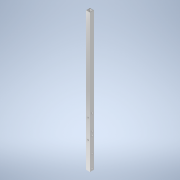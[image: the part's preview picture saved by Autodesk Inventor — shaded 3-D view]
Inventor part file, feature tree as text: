
AUTODESK INVENTOR PART (.ipt)
format: ipt  version: 2020.3 (Build 243373000, 373)  size: 172,544 bytes
history: native  units: mm
features: sketch x7, hole x4, extrude x3, other x1
ambient origin geometry x8: Origin, YZ Plane, XZ Plane, XY Plane, X Axis, Y Axis, Z Axis, Center Point
bodies: Body1 (feature_tree)
feature tree (15):
  other  "ソリッド1"
  extrude  "押し出し1"  Depth=9.0mm
  hole  "穴1"  [1 undecoded]
  hole  "穴2"  [1 undecoded]
  hole  "穴3"  [1 undecoded]
  extrude  "押し出し2"  Depth=1.2mm
  extrude  "押し出し3"  Depth=1.2mm
  hole  "穴4"  [1 undecoded]
  sketch  "スケッチ1"
  sketch  "スケッチ2"
  sketch  "スケッチ3"
  sketch  "スケッチ4"
  sketch  "スケッチ5"
  sketch  "スケッチ6"
  sketch  "スケッチ7"
note: 4 required parameter values undecoded (feature->parameter linkage not recoverable at this tier; creation-order binding heuristic only, values carry confidence <= 0.55)
